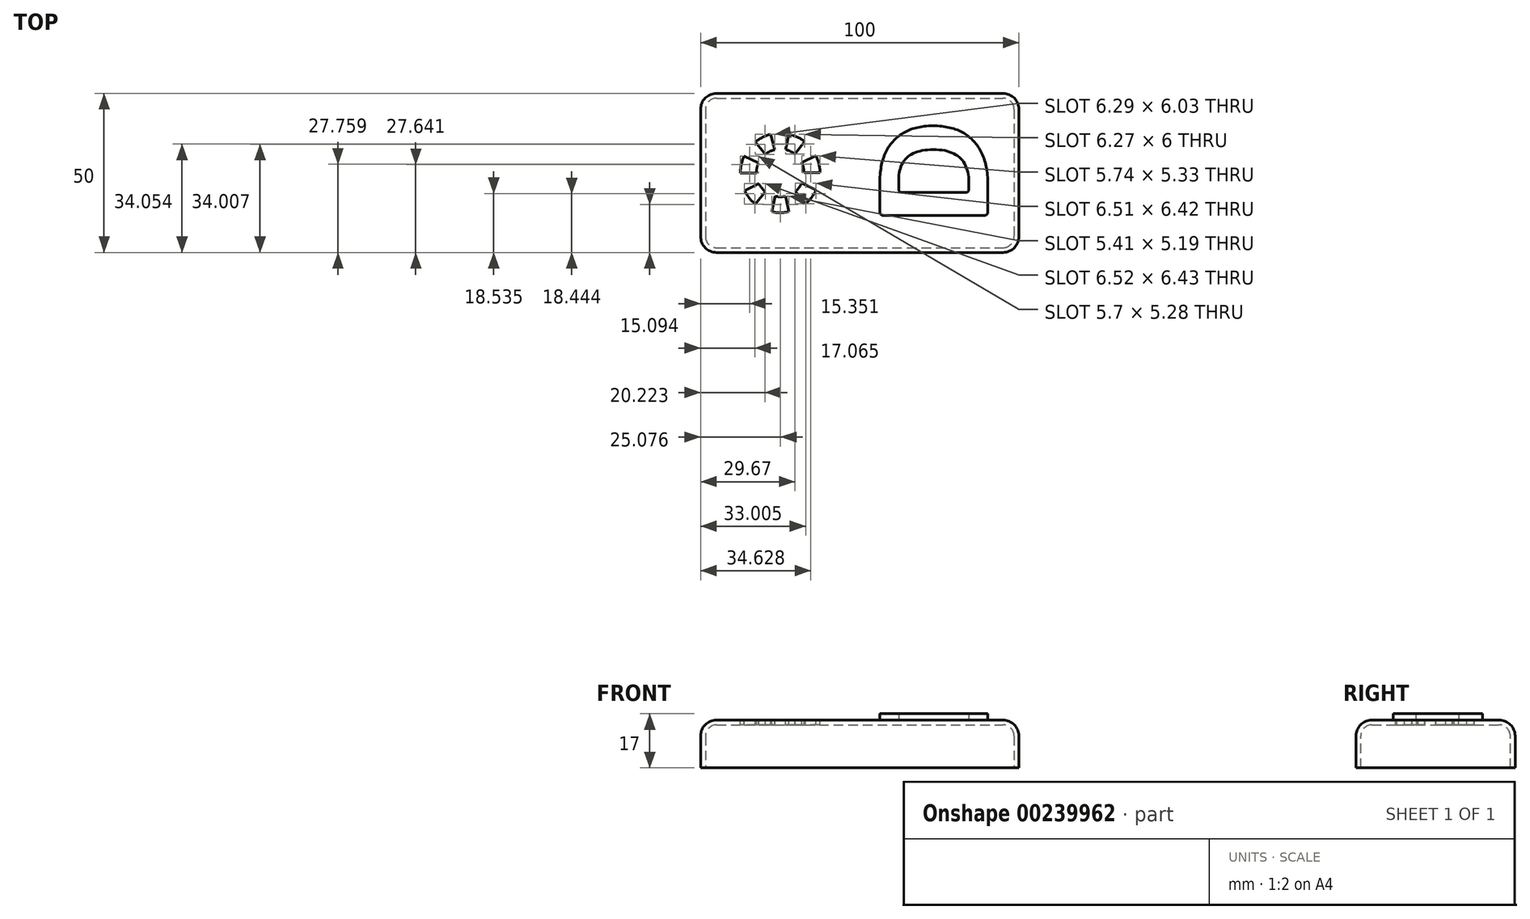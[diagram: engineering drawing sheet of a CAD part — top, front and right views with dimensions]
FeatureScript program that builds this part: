
annotation { "Feature Type Name" : "Feature", "Feature Type Description" : "" }
export const myFeature = defineFeature(function(context is Context, id is Id, definition is map)
    precondition{}
    {
        {
            var Q0;
            Q0=qCreatedBy(makeId("Top.planeOp"),FACE);
            var sketch = newSketch(context, id + "F0", { "sketchPlane" : qUnion([Q0])});
            skLineSegment(sketch, "E0.bottom", {"start": v(-45, 25) * mm, "end": v(45, 25) * mm});
            skLineSegment(sketch, "E0.top", {"start": v(-45, -25) * mm, "end": v(45, -25) * mm});
            skLineSegment(sketch, "E0.left", {"start": v(-50, 20) * mm, "end": v(-50, -20) * mm});
            skLineSegment(sketch, "E0.right", {"start": v(50, 20) * mm, "end": v(50, -20) * mm});
            skPoint(sketch, "E0.middle", {"position": v(0, 0) * mm});
            skPoint(sketch, "E1.visualSharp", {"position": v(-50, 25) * mm});
            skArc(sketch, "E1.filletArc", {"start": v(-45, 25) * mm, "mid": v(-48.54, 23.54) * mm, "end": v(-50, 20) * mm});
            skPoint(sketch, "E2.visualSharp", {"position": v(50, 25) * mm});
            skArc(sketch, "E2.filletArc", {"start": v(50, 20) * mm, "mid": v(48.54, 23.54) * mm, "end": v(45, 25) * mm});
            skPoint(sketch, "E3.visualSharp", {"position": v(50, -25) * mm});
            skArc(sketch, "E3.filletArc", {"start": v(45, -25) * mm, "mid": v(48.54, -23.54) * mm, "end": v(50, -20) * mm});
            skPoint(sketch, "E4.visualSharp", {"position": v(-50, -25) * mm});
            skArc(sketch, "E4.filletArc", {"start": v(-50, -20) * mm, "mid": v(-48.54, -23.54) * mm, "end": v(-45, -25) * mm});
            skSolve(sketch);
        }
        {
            var Q0;
            Q0=makeQuery(id+"F0.imprint","IMPRINT",FACE,{"disambiguationData":[TD([[makeQuery(id+"F0.imprint","IMPRINT",EDGE,{"derivedFrom":sQuery(id+"F0.wireOp",EDGE,"E0.bottom")}),-1.0]])]});
            extrude(context, id + "F1", {"entities" : qUnion([Q0]), "depth" : 15 * mm});
        }
        {
            var Q0;
            Q0=makeQuery(id+"F1.opExtrude","CAP_EDGE",EDGE,{"disambiguationData":[OSD([sQuery(id+"F0.wireOp",EDGE,"E0.top")])],"isStart":false});
            fillet(context, id + "F2", {"entities" : qUnion([Q0]), "radius" : 5 * mm, "tangentPropagation" : true, "allowEdgeOverflow" : false});
        }
        {
            var Q0;
            Q0=makeQuery(id+"F1.opExtrude","CAP_FACE",FACE,{"disambiguationData":[OSD([sQuery(id+"F0.wireOp",EDGE,"E0.bottom"),sQuery(id+"F0.wireOp",EDGE,"E0.top"),sQuery(id+"F0.wireOp",EDGE,"E0.left"),sQuery(id+"F0.wireOp",EDGE,"E0.right"),sQuery(id+"F0.wireOp",EDGE,"E1.filletArc"),sQuery(id+"F0.wireOp",EDGE,"E2.filletArc"),sQuery(id+"F0.wireOp",EDGE,"E3.filletArc"),sQuery(id+"F0.wireOp",EDGE,"E4.filletArc")])],"isStart":true});
            shell(context, id + "F3", {"entities" : qUnion([Q0]), "thickness" : 1.5 * mm});
        }
        {
            var Q0;
            Q0=makeQuery(id+"F1.opExtrude","CAP_FACE",FACE,{"disambiguationData":[OSD([sQuery(id+"F0.wireOp",EDGE,"E0.bottom"),sQuery(id+"F0.wireOp",EDGE,"E0.top"),sQuery(id+"F0.wireOp",EDGE,"E0.left"),sQuery(id+"F0.wireOp",EDGE,"E0.right"),sQuery(id+"F0.wireOp",EDGE,"E1.filletArc"),sQuery(id+"F0.wireOp",EDGE,"E2.filletArc"),sQuery(id+"F0.wireOp",EDGE,"E3.filletArc"),sQuery(id+"F0.wireOp",EDGE,"E4.filletArc")])],"isStart":false});
            var sketch = newSketch(context, id + "F4", { "sketchPlane" : qUnion([Q0])});
            skCircle(sketch, "E5", {"center": v(-25, 0) * mm, "radius": 12.5 * mm, "construction": true});
            skLineSegment(sketch, "E6", {"start": v(-25, 0) * mm, "end": v(-40.55, 0) * mm, "construction": true});
            skLineSegment(sketch, "E7", {"start": v(-25, 0) * mm, "end": v(-39.11, 6.58) * mm, "construction": true});
            skCircle(sketch, "E8", {"center": v(-25, 0) * mm, "radius": 7.5 * mm, "construction": true});
            skLineSegment(sketch, "E9", {"start": v(-37.5, 0) * mm, "end": v(-32.5, 0) * mm});
            skLineSegment(sketch, "E10", {"start": v(-31.8, 3.17) * mm, "end": v(-36.33, 5.28) * mm});
            skArc(sketch, "E11", {"start": v(-37.5, 0) * mm, "mid": v(-37.2, 2.7) * mm, "end": v(-36.33, 5.28) * mm});
            skArc(sketch, "E12", {"start": v(-32.5, 0) * mm, "mid": v(-32.32, 1.62) * mm, "end": v(-31.8, 3.17) * mm});
            skLineSegment(sketch, "E13.1.0", {"start": v(-32.8, -9.77) * mm, "end": v(-29.68, -5.86) * mm});
            skArc(sketch, "E13.1.1", {"start": v(-29.68, -5.86) * mm, "mid": v(-30.83, -4.71) * mm, "end": v(-31.72, -3.34) * mm});
            skLineSegment(sketch, "E13.1.2", {"start": v(-31.72, -3.34) * mm, "end": v(-36.2, -5.56) * mm});
            skArc(sketch, "E13.1.3", {"start": v(-32.8, -9.77) * mm, "mid": v(-34.72, -7.85) * mm, "end": v(-36.2, -5.56) * mm});
            skLineSegment(sketch, "E13.2.0", {"start": v(-22.22, -12.19) * mm, "end": v(-23.33, -7.31) * mm});
            skArc(sketch, "E13.2.1", {"start": v(-23.33, -7.31) * mm, "mid": v(-24.95, -7.5) * mm, "end": v(-26.58, -7.33) * mm});
            skLineSegment(sketch, "E13.2.2", {"start": v(-26.58, -7.33) * mm, "end": v(-27.63, -12.22) * mm});
            skArc(sketch, "E13.2.3", {"start": v(-22.22, -12.19) * mm, "mid": v(-24.92, -12.5) * mm, "end": v(-27.63, -12.22) * mm});
            skLineSegment(sketch, "E13.3.0", {"start": v(-13.74, -5.42) * mm, "end": v(-18.24, -3.25) * mm});
            skArc(sketch, "E13.3.1", {"start": v(-18.24, -3.25) * mm, "mid": v(-19.1, -4.64) * mm, "end": v(-20.25, -5.8) * mm});
            skLineSegment(sketch, "E13.3.2", {"start": v(-20.25, -5.8) * mm, "end": v(-17.09, -9.67) * mm});
            skArc(sketch, "E13.3.3", {"start": v(-13.74, -5.42) * mm, "mid": v(-15.18, -7.73) * mm, "end": v(-17.09, -9.67) * mm});
            skLineSegment(sketch, "E13.4.0", {"start": v(-13.74, 5.42) * mm, "end": v(-18.24, 3.25) * mm});
            skArc(sketch, "E13.4.1", {"start": v(-18.24, 3.25) * mm, "mid": v(-17.7, 1.71) * mm, "end": v(-17.5, 0.1) * mm});
            skLineSegment(sketch, "E13.4.2", {"start": v(-17.5, 0.1) * mm, "end": v(-12.5, 0.16) * mm});
            skArc(sketch, "E13.4.3", {"start": v(-13.74, 5.42) * mm, "mid": v(-12.83, 2.86) * mm, "end": v(-12.5, 0.16) * mm});
            skLineSegment(sketch, "E13.5.0", {"start": v(-22.22, 12.19) * mm, "end": v(-23.33, 7.31) * mm});
            skArc(sketch, "E13.5.1", {"start": v(-23.33, 7.31) * mm, "mid": v(-21.79, 6.78) * mm, "end": v(-20.4, 5.92) * mm});
            skLineSegment(sketch, "E13.5.2", {"start": v(-20.4, 5.92) * mm, "end": v(-17.33, 9.87) * mm});
            skArc(sketch, "E13.5.3", {"start": v(-22.22, 12.19) * mm, "mid": v(-19.65, 11.3) * mm, "end": v(-17.33, 9.87) * mm});
            skLineSegment(sketch, "E13.6.0", {"start": v(-32.8, 9.77) * mm, "end": v(-29.68, 5.86) * mm});
            skArc(sketch, "E13.6.1", {"start": v(-29.68, 5.86) * mm, "mid": v(-28.3, 6.74) * mm, "end": v(-26.76, 7.3) * mm});
            skLineSegment(sketch, "E13.6.2", {"start": v(-26.76, 7.3) * mm, "end": v(-27.93, 12.15) * mm});
            skArc(sketch, "E13.6.3", {"start": v(-32.8, 9.77) * mm, "mid": v(-30.5, 11.23) * mm, "end": v(-27.93, 12.15) * mm});
            skSolve(sketch);
        }
        {
            var Q0;
            Q0 = qSketchRegion(id + "F4", true);
            extrude(context, id + "F5", {"entities" : qUnion([Q0]), "operationType" : NewBodyOperationType.REMOVE, "endBound" : BoundingType.UP_TO_NEXT, "oppositeDirection" : true, "depth" : 25 * mm});
        }
        {
            var Q0;
            Q0=makeQuery(id+"F1.opExtrude","CAP_FACE",FACE,{"disambiguationData":[OSD([sQuery(id+"F0.wireOp",EDGE,"E0.bottom"),sQuery(id+"F0.wireOp",EDGE,"E0.top"),sQuery(id+"F0.wireOp",EDGE,"E0.left"),sQuery(id+"F0.wireOp",EDGE,"E0.right"),sQuery(id+"F0.wireOp",EDGE,"E1.filletArc"),sQuery(id+"F0.wireOp",EDGE,"E2.filletArc"),sQuery(id+"F0.wireOp",EDGE,"E3.filletArc"),sQuery(id+"F0.wireOp",EDGE,"E4.filletArc")])],"isStart":false});
            var sketch = newSketch(context, id + "F6", { "sketchPlane" : qUnion([Q0])});
            skText(sketch, "E14", { "text": "D", "fontName": "OpenSans-Bold.ttf"});
            const initialGuessF6  = {"E14": [0.04023, -0.0176, 0, 1, 0.0342]};
            skSetInitialGuess(sketch, initialGuessF6);
            skSolve(sketch);
        }
        {
            var Q0;
            Q0 = qSketchRegion(id + "F6", true);
            extrude(context, id + "F7", {"entities" : qUnion([Q0]), "operationType" : NewBodyOperationType.ADD, "depth" : 2 * mm});
        }
        {
            var Q0;
            Q0=makeQuery(id+"F7.opExtrude","SWEPT_EDGE",EDGE,{"disambiguationData":[OSD([sQuery(id+"F6.wireOp",EDGE,"E14.sketch_text.stroke-3"),sQuery(id+"F6.wireOp",EDGE,"E14.sketch_text.stroke-4")])]});
            var Q1;
            Q1=makeQuery(id+"F7.opExtrude","SWEPT_EDGE",EDGE,{"disambiguationData":[OSD([sQuery(id+"F6.wireOp",EDGE,"E14.sketch_text.stroke-2"),sQuery(id+"F6.wireOp",EDGE,"E14.sketch_text.stroke-3")])]});
            var Q2;
            Q2=makeQuery(id+"F7.opExtrude","SWEPT_EDGE",EDGE,{"disambiguationData":[OSD([sQuery(id+"F6.wireOp",EDGE,"E14.sketch_text.stroke-8"),sQuery(id+"F6.wireOp",EDGE,"E14.sketch_text.stroke-9")])]});
            var Q3;
            Q3=makeQuery(id+"F7.opExtrude","SWEPT_EDGE",EDGE,{"disambiguationData":[OSD([sQuery(id+"F6.wireOp",EDGE,"E14.sketch_text.stroke-9"),sQuery(id+"F6.wireOp",EDGE,"E14.sketch_text.stroke-10")])]});
            fillet(context, id + "F8", {"entities" : qUnion([Q0, Q1, Q2, Q3]), "radius" : 1 * mm, "tangentPropagation" : true, "allowEdgeOverflow" : false});
        }
    });
